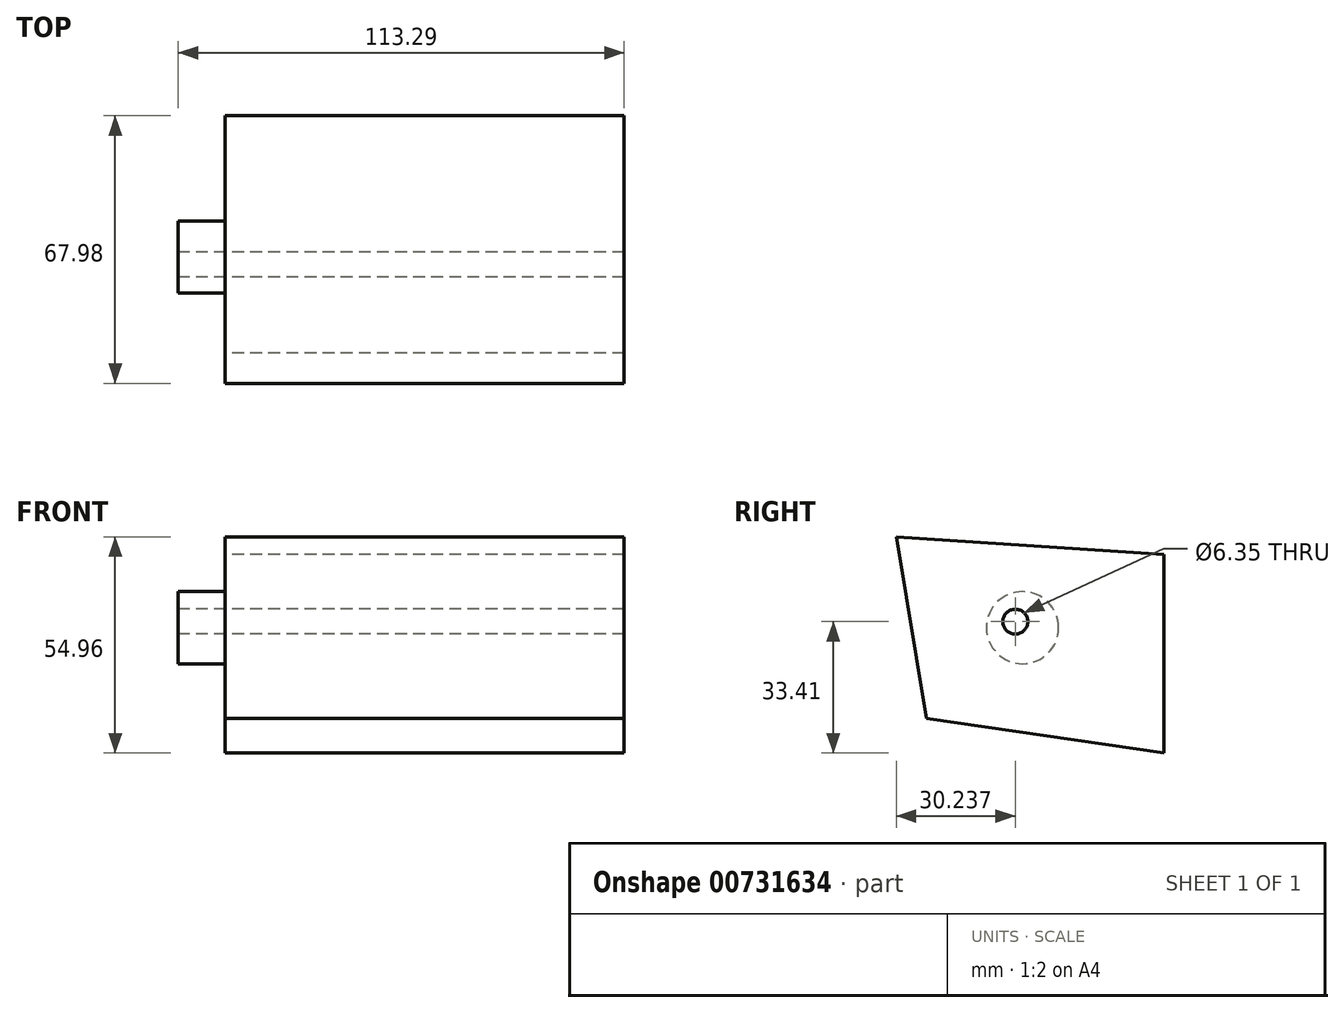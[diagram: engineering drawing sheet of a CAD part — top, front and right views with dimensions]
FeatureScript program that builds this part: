
annotation { "Feature Type Name" : "Feature", "Feature Type Description" : "" }
export const myFeature = defineFeature(function(context is Context, id is Id, definition is map)
    precondition{}
    {
        {
            var Q0;
            Q0=qCreatedBy(makeId("Right.planeOp"),FACE);
            var sketch = newSketch(context, id + "F0", { "sketchPlane" : qUnion([Q0])});
            skLineSegment(sketch, "E0", {"start": v(-49.27, 21.55) * mm, "end": v(18.71, 17.1) * mm});
            skLineSegment(sketch, "E1", {"start": v(18.71, 17.1) * mm, "end": v(18.71, -33.4) * mm});
            skLineSegment(sketch, "E2", {"start": v(18.71, -33.4) * mm, "end": v(-41.63, -24.6) * mm});
            skLineSegment(sketch, "E3", {"start": v(-41.63, -24.6) * mm, "end": v(-49.27, 21.55) * mm});
            skSolve(sketch);
        }
        {
            var Q0;
            Q0 = qSketchRegion(id + "F0", true);
            extrude(context, id + "F1", {"entities" : qUnion([Q0]), "depth" : 101.35 * mm, "offsetDistance" : 25.4 * mm});
        }
        {
            var Q0;
            Q0=makeQuery(id+"F1.opExtrude","CAP_FACE",FACE,{"disambiguationData":[OSD([sQuery(id+"F0.wireOp",EDGE,"E0"),sQuery(id+"F0.wireOp",EDGE,"E1"),sQuery(id+"F0.wireOp",EDGE,"E2"),sQuery(id+"F0.wireOp",EDGE,"E3")])],"isStart":false});
            var sketch = newSketch(context, id + "F2", { "sketchPlane" : qUnion([Q0])});
            skCircle(sketch, "E4", {"center": v(-17.19, -1.53) * mm, "radius": 9.16 * mm});
            skPoint(sketch, "E4.centerSnap0", {"position": v(-45.45, -1.53) * mm});
            skSolve(sketch);
        }
        {
            var Q0;
            Q0 = qSketchRegion(id + "F2", true);
            extrude(context, id + "F3", {"entities" : qUnion([Q0]), "operationType" : NewBodyOperationType.ADD, "oppositeDirection" : true, "depth" : 113.28 * mm, "offsetDistance" : 25.4 * mm});
        }
        {
            var Q0;
            Q0=makeQuery(id+"F3.opExtrude","CAP_FACE",FACE,{"disambiguationData":[OSD([sQuery(id+"F2.wireOp",EDGE,"E4")])],"isStart":false});
            var sketch = newSketch(context, id + "F4", { "sketchPlane" : qUnion([Q0])});
            skCircle(sketch, "E5", {"center": v(19.03, 0) * mm, "radius": 2.88 * mm});
            skSolve(sketch);
        }
        {
            var Q0;
            Q0=sQuery(id+"F4.wireOp",VERTEX,"E5.center");
            var Q1;
            Q1=makeQuery(id+"F1.opExtrude","SWEPT_BODY",BODY,{"disambiguationData":[OSD([sQuery(id+"F0.wireOp",EDGE,"E0"),sQuery(id+"F0.wireOp",EDGE,"E1"),sQuery(id+"F0.wireOp",EDGE,"E2"),sQuery(id+"F0.wireOp",EDGE,"E3")])]});
            hole(context, id + "F5", {"style" : HoleStyle.SIMPLE, "endStyle" : HoleEndStyle.THROUGH, "holeDiameter" : 6.35 * mm, "majorDiameter" : 6.35 * mm, "isTappedThrough" : true, "tappedDepth" : 12.7 * mm, "tapClearance" : 3, "locations" : qUnion([Q0]), "scope" : qUnion([Q1])});
        }
    });
